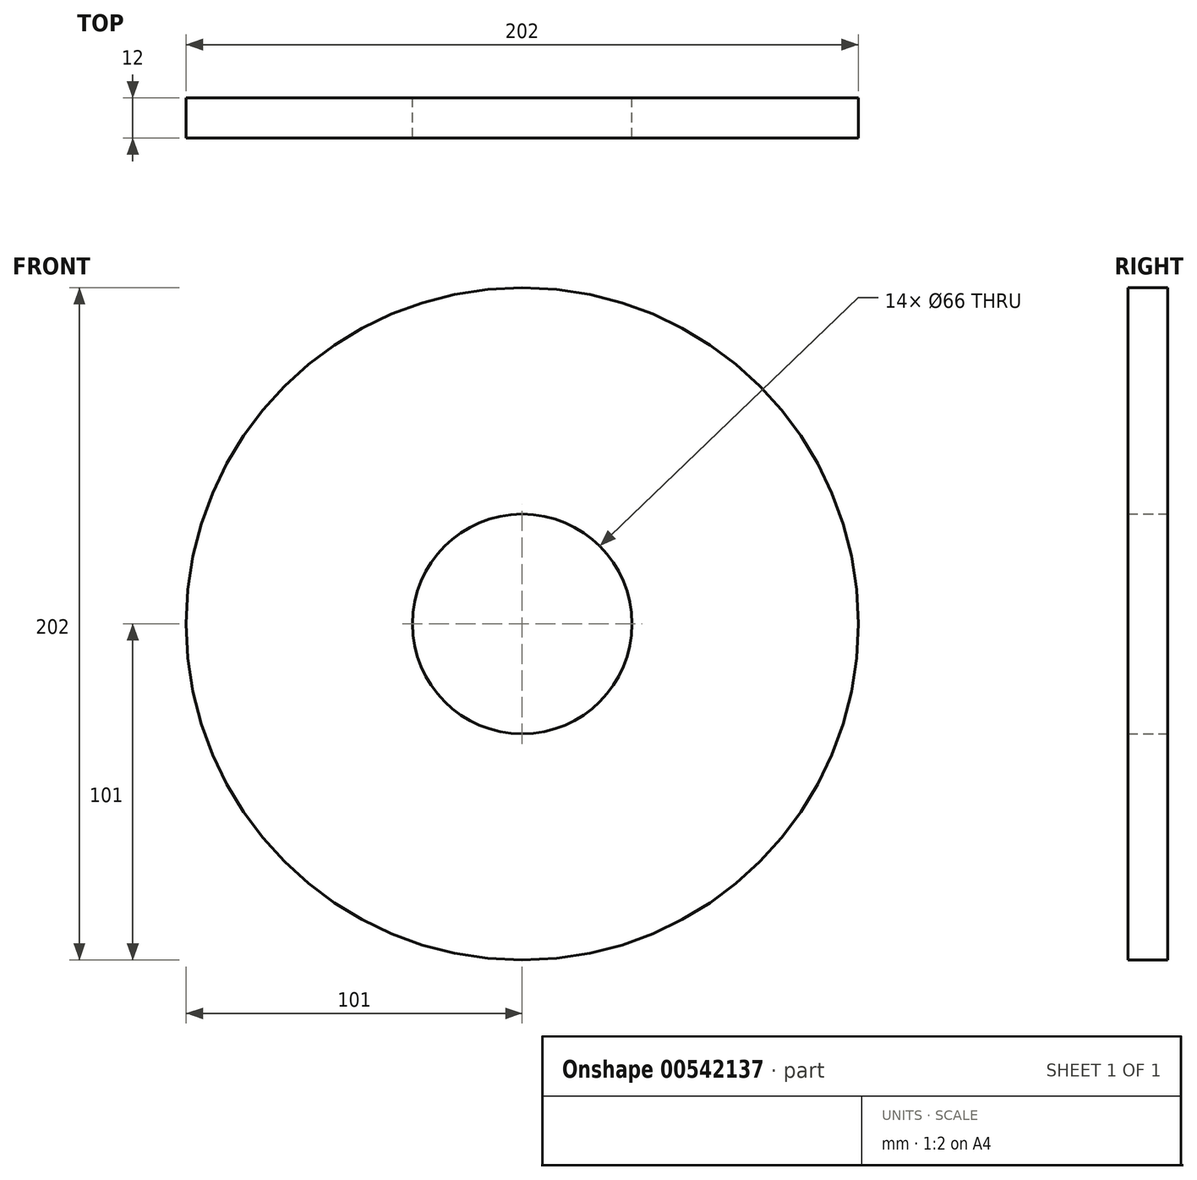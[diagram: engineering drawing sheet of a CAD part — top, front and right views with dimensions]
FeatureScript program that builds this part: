
annotation { "Feature Type Name" : "Feature", "Feature Type Description" : "" }
export const myFeature = defineFeature(function(context is Context, id is Id, definition is map)
    precondition{}
    {
        {
            var Q0;
            Q0=qCreatedBy(makeId("Front.planeOp"),FACE);
            var sketch = newSketch(context, id + "F0", { "sketchPlane" : qUnion([Q0])});
            skCircle(sketch, "E0", {"center": v(0, 0) * mm, "radius": 33 * mm});
            skCircle(sketch, "E1", {"center": v(0, 0) * mm, "radius": 101 * mm});
            skSolve(sketch);
        }
        {
            var Q0;
            Q0=makeQuery(id+"F0.imprint","IMPRINT",FACE,{"disambiguationData":[TD([[makeQuery(id+"F0.imprint","IMPRINT",EDGE,{"derivedFrom":sQuery(id+"F0.wireOp",EDGE,"E0")}),-1.0]])]});
            extrude(context, id + "F1", {"entities" : qUnion([Q0]), "depth" : 12 * mm, "offsetDistance" : 25 * mm});
        }
    });
